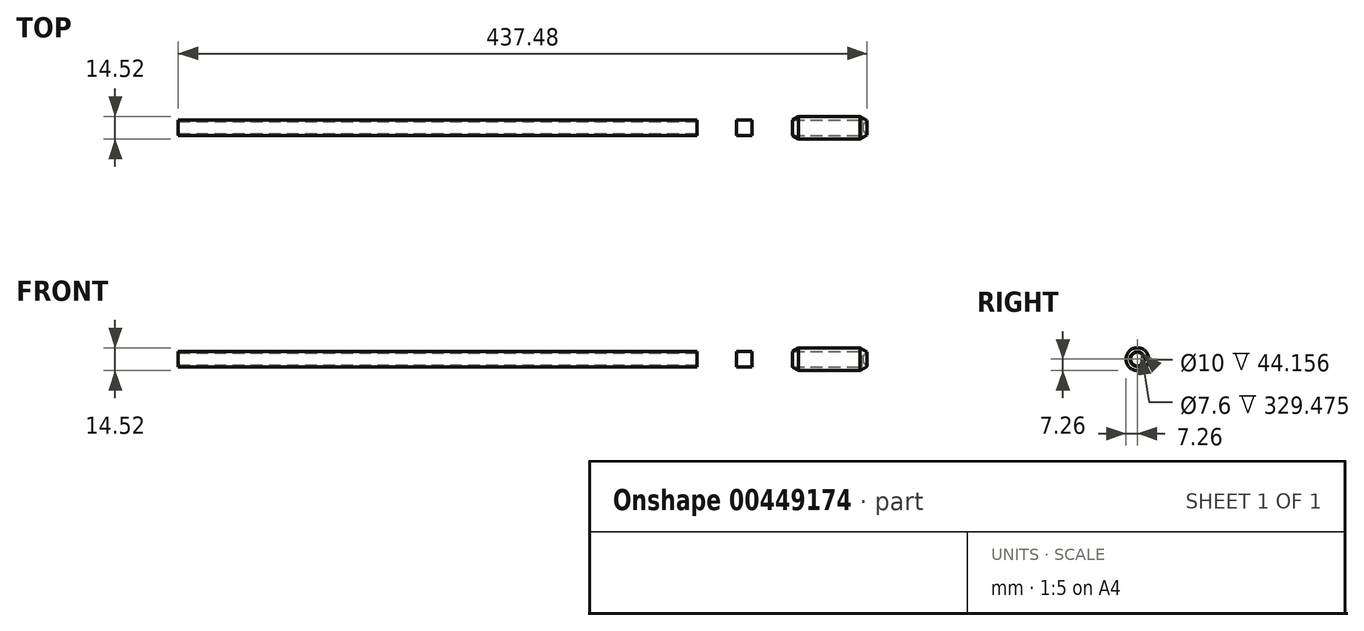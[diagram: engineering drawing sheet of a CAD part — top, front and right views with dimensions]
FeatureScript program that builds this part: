
annotation { "Feature Type Name" : "Feature", "Feature Type Description" : "" }
export const myFeature = defineFeature(function(context is Context, id is Id, definition is map)
    precondition{}
    {
        {
            var Q0;
            Q0=qCreatedBy(makeId("Front.planeOp"),FACE);
            var sketch = newSketch(context, id + "F0", { "sketchPlane" : qUnion([Q0]), "disableImprinting" : false});
            skLineSegment(sketch, "E0", {"start": v(0, -4.76) * mm, "end": v(0, -7.26) * mm, "construction": true});
            skLineSegment(sketch, "E1", {"start": v(0, -7.26) * mm, "end": v(-50, -7.26) * mm});
            skArc(sketch, "E2", {"start": v(-4.76, 0) * mm, "mid": v(-3.37, -3.37) * mm, "end": v(0, -4.76) * mm});
            skLineSegment(sketch, "E3", {"start": v(-5.26, -5) * mm, "end": v(-5.26, 0) * mm});
            skLineSegment(sketch, "E4", {"start": v(-4.76, 0) * mm, "end": v(-5.26, 0) * mm});
            skLineSegment(sketch, "E5", {"start": v(-5.26, -5) * mm, "end": v(-50, -5) * mm});
            skLineSegment(sketch, "E6", {"start": v(-50, -7.26) * mm, "end": v(-50, -5) * mm});
            skLineSegment(sketch, "E7.0", {"start": v(-2, -4.32) * mm, "end": v(-2, -7.26) * mm});
            skSolve(sketch);
        }
        {
            var Q0;
            Q0=makeQuery(id+"F0.imprint","IMPRINT",FACE,{"disambiguationData":[TD([[makeQuery(id+"F0.imprint","IMPRINT",EDGE,{"derivedFrom":sQuery(id+"F0.wireOp",EDGE,"E3")}),-1.0]])]});
            var Q1;
            Q1=sQuery(id+"F0.wireOp",EDGE,"E4");
            revolve(context, id + "F1", {"entities" : qUnion([Q0]), "axis" : qUnion([Q1]), "revolveType" : RevolveType.FULL});
        }
        {
            var Q0;
            Q0=makeQuery(id+"F1.opRevolve","SWEPT_FACE",FACE,{"disambiguationData":[OSD([sQuery(id+"F0.wireOp",EDGE,"E6")])]});
            cPlane(context, id + "F2", {"entities" : qUnion([Q0]), "cplaneType" : CPlaneType.OFFSET, "offset" : 25 * mm, "width" : 150 * mm, "height" : 150 * mm});
        }
        {
            var Q0;
            Q0=qCreatedBy(id+"F2.planeOp",FACE);
            var sketch = newSketch(context, id + "F3", { "sketchPlane" : qUnion([Q0])});
            skCircle(sketch, "E8.0", {"center": v(0, 0) * mm, "radius": 5 * mm});
            skSolve(sketch);
        }
        {
            var Q0;
            Q0=makeQuery(id+"F3.imprint","IMPRINT",FACE,{"disambiguationData":[TD([[makeQuery(id+"F3.imprint","IMPRINT",EDGE,{"derivedFrom":sQuery(id+"F3.wireOp",EDGE,"E8.0")}),1.0]])]});
            extrude(context, id + "F4", {"entities" : qUnion([Q0]), "depth" : 10 * mm});
        }
        {
            var Q0;
            Q0=makeQuery(id+"F4.opExtrude","CAP_FACE",FACE,{"disambiguationData":[OSD([sQuery(id+"F3.wireOp",EDGE,"E8.0")])],"isStart":false});
            cPlane(context, id + "F5", {"entities" : qUnion([Q0]), "cplaneType" : CPlaneType.OFFSET, "offset" : 25 * mm, "width" : 150 * mm, "height" : 150 * mm});
        }
        {
            var Q0;
            Q0=qCreatedBy(id+"F5.planeOp",FACE);
            var sketch = newSketch(context, id + "F6", { "sketchPlane" : qUnion([Q0])});
            skCircle(sketch, "E9.0", {"center": v(0, 0) * mm, "radius": 5 * mm});
            skCircle(sketch, "E10", {"center": v(0, 0) * mm, "radius": 3.8 * mm});
            skSolve(sketch);
        }
        {
            var Q0;
            Q0=makeQuery(id+"F6.imprint","IMPRINT",FACE,{"disambiguationData":[TD([[makeQuery(id+"F6.imprint","IMPRINT",EDGE,{"derivedFrom":sQuery(id+"F6.wireOp",EDGE,"E9.0")}),1.0]])]});
            extrude(context, id + "F7", {"entities" : qUnion([Q0]), "depth" : 329.48 * mm});
        }
        {
            var Q0;
            Q0=makeQuery(id+"F1.opRevolve","SWEPT_EDGE",EDGE,{"disambiguationData":[OSD([sQuery(id+"F0.wireOp",EDGE,"E0"),sQuery(id+"F0.wireOp",EDGE,"E1")])]});
            chamfer(context, id + "F8", {"entities" : qUnion([Q0]), "chamferType" : ChamferType.OFFSET_ANGLE, "width" : 4.5 * mm, "oppositeDirection" : false, "angle" : 30 * degree, "tangentPropagation" : true});
        }
    });
